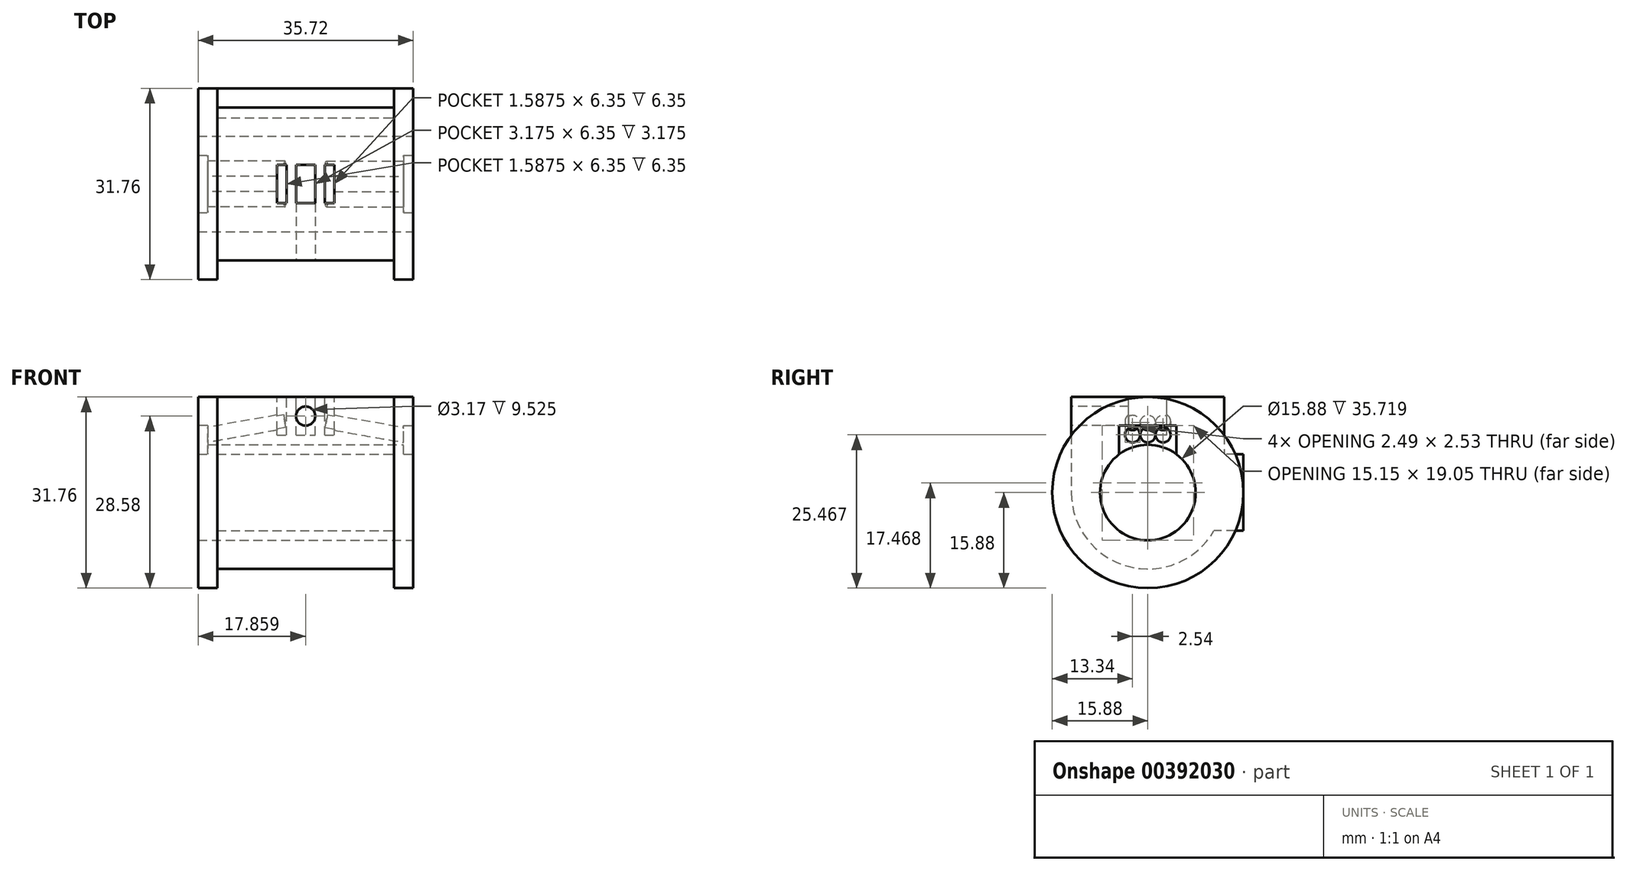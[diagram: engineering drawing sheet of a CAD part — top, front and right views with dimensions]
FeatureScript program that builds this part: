
annotation { "Feature Type Name" : "Feature", "Feature Type Description" : "" }
export const myFeature = defineFeature(function(context is Context, id is Id, definition is map)
    precondition{}
    {
        {
            var Q0;
            Q0=qCreatedBy(makeId("Right.planeOp"),FACE);
            var sketch = newSketch(context, id + "F0", { "sketchPlane" : qUnion([Q0])});
            skCircle(sketch, "E0", {"center": v(0, 0) * mm, "radius": 15.88 * mm});
            skSolve(sketch);
        }
        {
            var Q0;
            Q0 = qSketchRegion(id + "F0", true);
            extrude(context, id + "F1", {"entities" : qUnion([Q0]), "depth" : 35.72 * mm});
        }
        {
            var Q0;
            Q0=qCreatedBy(makeId("Front.planeOp"),FACE);
            var sketch = newSketch(context, id + "F2", { "sketchPlane" : qUnion([Q0])});
            skLineSegment(sketch, "E1.bottom", {"start": v(3.18, 15.88) * mm, "end": v(32.54, 15.88) * mm});
            skLineSegment(sketch, "E1.top", {"start": v(3.18, 12.7) * mm, "end": v(32.54, 12.7) * mm});
            skLineSegment(sketch, "E1.left", {"start": v(3.18, 15.88) * mm, "end": v(3.18, 12.7) * mm});
            skLineSegment(sketch, "E1.right", {"start": v(32.54, 15.88) * mm, "end": v(32.54, 12.7) * mm});
            skLineSegment(sketch, "E2", {"start": v(0, 0) * mm, "end": v(38.32, 0) * mm, "construction": true});
            skSolve(sketch);
        }
        {
            var Q0;
            Q0 = qSketchRegion(id + "F2", true);
            var Q1;
            Q1=sQuery(id+"F2.wireOp",EDGE,"E2");
            revolve(context, id + "F3", {"operationType" : NewBodyOperationType.REMOVE, "entities" : qUnion([Q0]), "axis" : qUnion([Q1]), "revolveType" : RevolveType.FULL, "oppositeDirection" : true});
        }
        {
            var Q0;
            Q0=qCreatedBy(makeId("Top.planeOp"),FACE);
            var sketch = newSketch(context, id + "F4", { "sketchPlane" : qUnion([Q0])});
            skLineSegment(sketch, "E3.bottom", {"start": v(3.18, 12.7) * mm, "end": v(32.54, 12.7) * mm});
            skLineSegment(sketch, "E3.top", {"start": v(3.18, -12.7) * mm, "end": v(32.54, -12.7) * mm});
            skLineSegment(sketch, "E3.left", {"start": v(3.18, 12.7) * mm, "end": v(3.18, -12.7) * mm});
            skLineSegment(sketch, "E3.right", {"start": v(32.54, 12.7) * mm, "end": v(32.54, -12.7) * mm});
            skSolve(sketch);
        }
        {
            var Q0;
            Q0 = qSketchRegion(id + "F4", true);
            extrude(context, id + "F5", {"entities" : qUnion([Q0]), "operationType" : NewBodyOperationType.ADD, "depth" : 15.88 * mm});
        }
        {
            var Q0;
            Q0=qCreatedBy(makeId("Front.planeOp"),FACE);
            var sketch = newSketch(context, id + "F6", { "sketchPlane" : qUnion([Q0])});
            skLineSegment(sketch, "E4.bottom", {"start": v(32.54, 6.35) * mm, "end": v(3.18, 6.35) * mm});
            skLineSegment(sketch, "E4.top", {"start": v(32.54, -6.35) * mm, "end": v(3.18, -6.35) * mm});
            skLineSegment(sketch, "E4.left", {"start": v(32.54, 6.35) * mm, "end": v(32.54, -6.35) * mm});
            skLineSegment(sketch, "E4.right", {"start": v(3.18, 6.35) * mm, "end": v(3.18, -6.35) * mm});
            skSolve(sketch);
        }
        {
            var Q0;
            Q0 = qSketchRegion(id + "F6", true);
            extrude(context, id + "F7", {"entities" : qUnion([Q0]), "operationType" : NewBodyOperationType.ADD, "oppositeDirection" : true, "depth" : 15.88 * mm});
        }
        {
            var Q0;
            Q0=makeQuery(id+"F1.opExtrude","CAP_FACE",FACE,{"disambiguationData":[OSD([sQuery(id+"F0.wireOp",EDGE,"E0")])],"isStart":false});
            var sketch = newSketch(context, id + "F8", { "sketchPlane" : qUnion([Q0])});
            skCircle(sketch, "E5", {"center": v(0, 0) * mm, "radius": 7.94 * mm});
            skSolve(sketch);
        }
        {
            var Q0;
            Q0 = qSketchRegion(id + "F8", true);
            extrude(context, id + "F9", {"entities" : qUnion([Q0]), "operationType" : NewBodyOperationType.REMOVE, "endBound" : BoundingType.THROUGH_ALL, "oppositeDirection" : true, "depth" : 25.4 * mm});
        }
        {
            var Q0;
            Q0=makeQuery(id+"F5.opExtrude","CAP_FACE",FACE,{"disambiguationData":[OSD([sQuery(id+"F4.wireOp",EDGE,"E3.bottom"),sQuery(id+"F4.wireOp",EDGE,"E3.top"),sQuery(id+"F4.wireOp",EDGE,"E3.left"),sQuery(id+"F4.wireOp",EDGE,"E3.right")])],"isStart":false});
            var sketch = newSketch(context, id + "F10", { "sketchPlane" : qUnion([Q0])});
            skLineSegment(sketch, "E6.bottom", {"start": v(13.1, 3.17) * mm, "end": v(14.68, 3.17) * mm});
            skLineSegment(sketch, "E6.top", {"start": v(13.1, -3.17) * mm, "end": v(14.68, -3.17) * mm});
            skLineSegment(sketch, "E6.left", {"start": v(13.1, 3.18) * mm, "end": v(13.1, -3.17) * mm});
            skLineSegment(sketch, "E6.right", {"start": v(14.68, 3.18) * mm, "end": v(14.68, -3.17) * mm});
            skLineSegment(sketch, "E7.bottom", {"start": v(16.27, 3.18) * mm, "end": v(19.45, 3.18) * mm});
            skLineSegment(sketch, "E7.top", {"start": v(16.27, -3.17) * mm, "end": v(19.45, -3.17) * mm});
            skLineSegment(sketch, "E7.left", {"start": v(16.27, 3.18) * mm, "end": v(16.27, -3.17) * mm});
            skLineSegment(sketch, "E7.right", {"start": v(19.45, 3.18) * mm, "end": v(19.45, -3.17) * mm});
            skLineSegment(sketch, "E8.bottom", {"start": v(21.03, 3.17) * mm, "end": v(22.62, 3.17) * mm});
            skLineSegment(sketch, "E8.top", {"start": v(21.03, -3.17) * mm, "end": v(22.62, -3.17) * mm});
            skLineSegment(sketch, "E8.left", {"start": v(21.03, 3.18) * mm, "end": v(21.03, -3.17) * mm});
            skLineSegment(sketch, "E8.right", {"start": v(22.62, 3.18) * mm, "end": v(22.62, -3.17) * mm});
            skSolve(sketch);
        }
        {
            var Q0;
            Q0 = qSketchRegion(id + "F10", true);
            extrude(context, id + "F11", {"entities" : qUnion([Q0]), "operationType" : NewBodyOperationType.REMOVE, "oppositeDirection" : true, "depth" : 6.35 * mm});
        }
        {
            var Q0;
            Q0=makeQuery(id+"F5.opExtrude","SWEPT_FACE",FACE,{"disambiguationData":[OSD([sQuery(id+"F4.wireOp",EDGE,"E3.top")])]});
            var sketch = newSketch(context, id + "F12", { "sketchPlane" : qUnion([Q0])});
            skCircle(sketch, "E9", {"center": v(17.86, 12.7) * mm, "radius": 1.59 * mm});
            skSolve(sketch);
        }
        {
            var Q0;
            Q0 = qSketchRegion(id + "F12", true);
            extrude(context, id + "F13", {"entities" : qUnion([Q0]), "operationType" : NewBodyOperationType.REMOVE, "oppositeDirection" : true, "depth" : 12.7 * mm});
        }
        {
            var Q0;
            Q0=makeQuery(id+"F1.opExtrude","CAP_FACE",FACE,{"disambiguationData":[OSD([sQuery(id+"F0.wireOp",EDGE,"E0")])],"isStart":false});
            var sketch = newSketch(context, id + "F14", { "sketchPlane" : qUnion([Q0])});
            skSolve(sketch);
        }
        {
            var Q0;
            Q0=makeQuery(id+"F14.imprint","IMPRINT",FACE,{"disambiguationData":[TD([[makeQuery(id+"F14.imprint","IMPRINT",EDGE,{"derivedFrom":makeQuery(id+"F1.opExtrude","CAP_EDGE",EDGE,{"disambiguationData":[OSD([sQuery(id+"F0.wireOp",EDGE,"E0")])],"isStart":false})}),1.0]])]});
            var sketch = newSketch(context, id + "F15", { "sketchPlane" : qUnion([Q0])});
            skLineSegment(sketch, "E10.bottom", {"start": v(-4.76, 5.08) * mm, "end": v(4.76, 5.08) * mm});
            skLineSegment(sketch, "E10.top", {"start": v(-4.76, 11.11) * mm, "end": v(4.76, 11.11) * mm});
            skLineSegment(sketch, "E10.left", {"start": v(-4.76, 5.08) * mm, "end": v(-4.76, 11.11) * mm});
            skLineSegment(sketch, "E10.right", {"start": v(4.76, 5.08) * mm, "end": v(4.76, 11.11) * mm});
            skSolve(sketch);
        }
        {
            var Q0;
            Q0 = qSketchRegion(id + "F15", true);
            extrude(context, id + "F16", {"entities" : qUnion([Q0]), "operationType" : NewBodyOperationType.REMOVE, "oppositeDirection" : true, "depth" : 1.59 * mm});
        }
        {
            var Q0;
            Q0=makeQuery(id+"F1.opExtrude","CAP_FACE",FACE,{"disambiguationData":[OSD([sQuery(id+"F0.wireOp",EDGE,"E0")])],"isStart":true});
            var sketch = newSketch(context, id + "F17", { "sketchPlane" : qUnion([Q0])});
            skLineSegment(sketch, "E11.bottom", {"start": v(-4.76, 11.11) * mm, "end": v(4.76, 11.11) * mm});
            skLineSegment(sketch, "E11.top", {"start": v(-4.76, 5.08) * mm, "end": v(4.76, 5.08) * mm});
            skLineSegment(sketch, "E11.left", {"start": v(-4.76, 11.11) * mm, "end": v(-4.76, 5.08) * mm});
            skLineSegment(sketch, "E11.right", {"start": v(4.76, 11.11) * mm, "end": v(4.76, 5.08) * mm});
            skSolve(sketch);
        }
        {
            var Q0;
            Q0 = qSketchRegion(id + "F17", true);
            extrude(context, id + "F18", {"entities" : qUnion([Q0]), "operationType" : NewBodyOperationType.REMOVE, "oppositeDirection" : true, "depth" : 1.59 * mm});
        }
        {
            var Q0;
            Q0=makeQuery(id+"F14.imprint","IMPRINT",FACE,{"disambiguationData":[TD([[makeQuery(id+"F14.imprint","IMPRINT",EDGE,{"derivedFrom":makeQuery(id+"F1.opExtrude","CAP_EDGE",EDGE,{"disambiguationData":[OSD([sQuery(id+"F0.wireOp",EDGE,"E0")])],"isStart":false})}),1.0]])]});
            cPlane(context, id + "F19", {"entities" : qUnion([Q0]), "cplaneType" : CPlaneType.OFFSET, "offset" : 0.76 * mm, "oppositeDirection" : true, "width" : 152.4 * mm, "height" : 152.4 * mm});
        }
        {
            var Q0;
            Q0=qCreatedBy(id+"F19.planeOp",FACE);
            var sketch = newSketch(context, id + "F20", { "sketchPlane" : qUnion([Q0])});
            skLineSegment(sketch, "E12", {"start": v(-2.22, 8.83) * mm, "end": v(2.22, 8.83) * mm});
            skSolve(sketch);
        }
        {
            var Q0;
            Q0=sQuery(id+"F20.wireOp",EDGE,"E12");
            cPlane(context, id + "F21", {"entities" : qUnion([Q0]), "cplaneType" : CPlaneType.LINE_ANGLE, "offset" : 25.4 * mm, "angle" : 100 * degree, "width" : 152.4 * mm, "height" : 152.4 * mm});
        }
        {
            var Q0;
            Q0=qCreatedBy(id+"F21.planeOp",FACE);
            var sketch = newSketch(context, id + "F22", { "sketchPlane" : qUnion([Q0])});
            skCircle(sketch, "E13", {"center": v(2.54, 15.37) * mm, "radius": 1.24 * mm});
            skCircle(sketch, "E14", {"center": v(0, 15.37) * mm, "radius": 1.24 * mm});
            skCircle(sketch, "E15", {"center": v(-2.54, 15.37) * mm, "radius": 1.24 * mm});
            skSolve(sketch);
        }
        {
            var Q0;
            Q0 = qSketchRegion(id + "F22", true);
            extrude(context, id + "F23", {"entities" : qUnion([Q0]), "operationType" : NewBodyOperationType.REMOVE, "oppositeDirection" : true, "depth" : 13.97 * mm});
        }
        {
            var Q0;
            Q0=makeQuery(id+"F1.opExtrude","CAP_FACE",FACE,{"disambiguationData":[OSD([sQuery(id+"F0.wireOp",EDGE,"E0")])],"isStart":true});
            cPlane(context, id + "F24", {"entities" : qUnion([Q0]), "cplaneType" : CPlaneType.OFFSET, "offset" : 0.76 * mm, "oppositeDirection" : true, "width" : 152.4 * mm, "height" : 152.4 * mm});
        }
        {
            var Q0;
            Q0=qCreatedBy(id+"F24.planeOp",FACE);
            var sketch = newSketch(context, id + "F25", { "sketchPlane" : qUnion([Q0])});
            skLineSegment(sketch, "E16", {"start": v(-3.5, 8.83) * mm, "end": v(3.5, 8.83) * mm});
            skSolve(sketch);
        }
        {
            var Q0;
            Q0=sQuery(id+"F25.wireOp",EDGE,"E16");
            cPlane(context, id + "F26", {"entities" : qUnion([Q0]), "cplaneType" : CPlaneType.LINE_ANGLE, "offset" : 25.4 * mm, "angle" : 100 * degree, "width" : 152.4 * mm, "height" : 152.4 * mm});
        }
        {
            var Q0;
            Q0=qCreatedBy(id+"F26.planeOp",FACE);
            var sketch = newSketch(context, id + "F27", { "sketchPlane" : qUnion([Q0])});
            skCircle(sketch, "E17", {"center": v(2.54, 9.17) * mm, "radius": 1.24 * mm});
            skCircle(sketch, "E18", {"center": v(-2.54, 9.17) * mm, "radius": 1.24 * mm});
            skCircle(sketch, "E19", {"center": v(0, 9.17) * mm, "radius": 1.24 * mm});
            skSolve(sketch);
        }
        {
            var Q0;
            Q0 = qSketchRegion(id + "F27", true);
            extrude(context, id + "F28", {"entities" : qUnion([Q0]), "operationType" : NewBodyOperationType.REMOVE, "depth" : 13.97 * mm});
        }
    });
